# Revit family: NEVA 3.0
name_source: partatom
category: Lighting Fixtures
units: mm (PartAtom-declared; Revit-internal decimal feet)

## family parameters
Always vertical = No
Cut with Voids When Loaded = No
Light Source = No
OmniClass Number = 23.80.70.00
OmniClass Title = Lighting
Part Type = Normal
Room Calculation Point = Yes
Round Connector Dimension = Use Diameter
Shared = No
Work Plane-Based = Yes

## types (4) — shared parameters
Apparent Load Phase 1 = 5 W
Base = L&L_Anticorodal aluminium
Body = L&L_Anticorodal aluminium
CRI = CRI 80
Code = -
Control system = ON/OFF, 0-10V
Cutout dimensions = -
Default Elevation = 1219 mm
Delivered lumen output = 1610 lm (3000K, 30°)
Description = Linear profile for outdoor applications
Energy efficiency class = A A+ A++
Features = Easy to wire. The electrical cables can be attached directly to the connector, making the product easier to install
Geometry = NEVA 3.0 Movable_A
H1 = 29 mm  [stored 0.0951444 ft]
Height mm = 29 mm  [stored 0.0951444 ft]
IP = IP65, IP67
LED Colour = 2000K, 3000K, 4000K
Length mm = 616 mm  [stored 2.021 ft]
Lens = L&L_Tempered extra-clear glass
Lumen output at source = 2570 lm (3000K)
Manufacturer = L&L Luce&Light
Material = body in black-anodized anticorodal aluminium,  screen in serigraphed, transparent and tempered extra-clear glass
Model = Neva 3.0
Mounting = surface mounted (ceiling, wall, floor) with brackets or recessed (ceiling, floor, wall) with outer casing
No. and type of led = 10 power LEDs pitch 60 mm, 3-step MacAdam, 50 000h L85 B10 (Ta 25°C)
Notes = -
Power = 23W
Power Supply = L&L_Black Anodized aluminium
Power cables = -
Power supply = 230Vac
Power supply unit = built-in
not included
not included
URL = https://www.lucelight.it
URL Accessories and power supply units = https://www.lucelight.it
URL Catalogue = https://www.lucelight.it
URL DXF = https://www.lucelight.it
URL Description = https://www.lucelight.it
URL General code = https://www.lucelight.it
URL IES Photometric file = https://www.lucelight.it
URL Image = https://www.lucelight.it
URL Technical sheet = https://www.lucelight.it
Vertical rotation max = 90.00°
Weight kg = 1.60 kg
Width mm = 37 mm  [stored 0.121391 ft]
Wiring = parallel
X1 = 500 mm

## per-type parameters (varying)
| type | Light source | Optics |
| NEVA 3.0 S 11° | Light source Pivot : S 11° | 11° |
| NEVA 3.0 M 30° | Light source Pivot : M 30° | 30° |
| NEVA 3.0 L 45° | Light source Pivot : L 45° | 45° |
| NEVA 3.0 W 10°x40° | Light source Pivot : W 10°x40° | 10°x40° |

note: [stored X ft] marks values corroborated as IEEE doubles in the binary element streams (Revit-internal decimal feet)

## geometry (parser evidence)
native form markers: Blend x4, Sweep x16
no freeform markers — native parametric forms only
